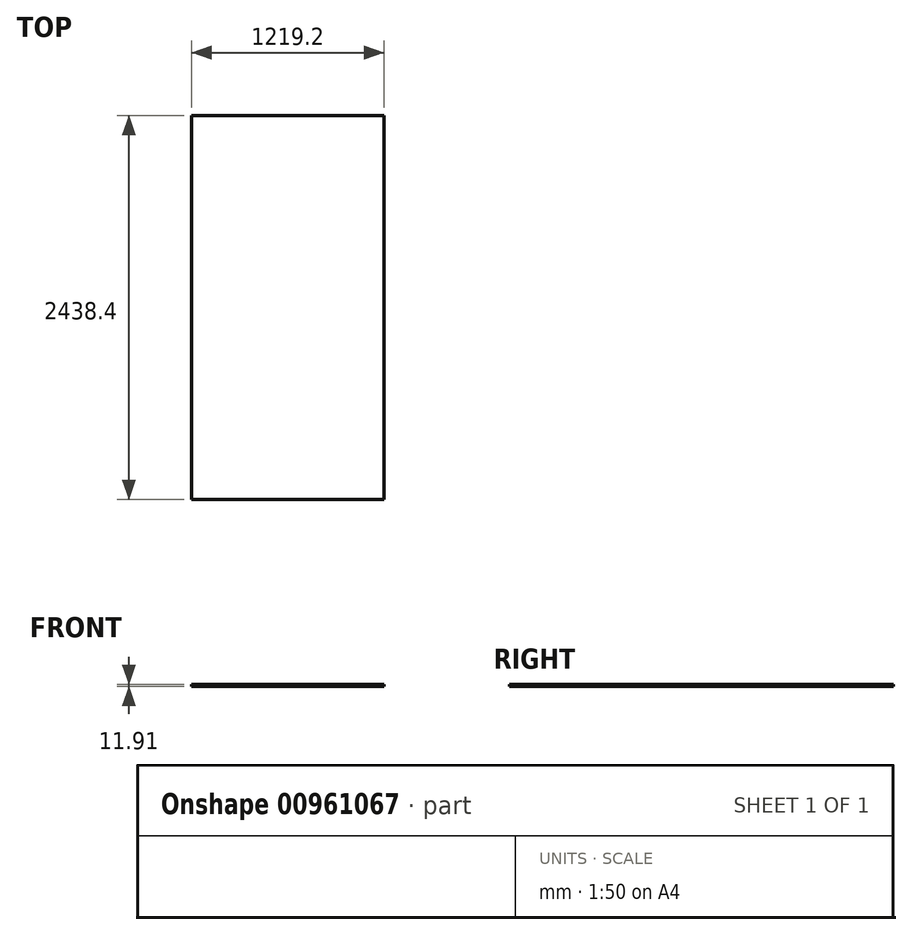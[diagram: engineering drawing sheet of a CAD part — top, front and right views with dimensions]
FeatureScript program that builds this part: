
annotation { "Feature Type Name" : "Feature", "Feature Type Description" : "" }
export const myFeature = defineFeature(function(context is Context, id is Id, definition is map)
    precondition{}
    {
        {
            var Q0;
            Q0=qCreatedBy(makeId("Front.planeOp"),FACE);
            var sketch = newSketch(context, id + "F0", { "sketchPlane" : qUnion([Q0])});
            skLineSegment(sketch, "E0.bottom", {"start": v(-366.63, 36.44) * mm, "end": v(852.57, 36.44) * mm});
            skLineSegment(sketch, "E0.top", {"start": v(-366.63, 48.35) * mm, "end": v(852.57, 48.35) * mm});
            skLineSegment(sketch, "E0.left", {"start": v(-366.63, 36.44) * mm, "end": v(-366.63, 48.35) * mm});
            skLineSegment(sketch, "E0.right", {"start": v(852.57, 36.44) * mm, "end": v(852.57, 48.35) * mm});
            skLineSegment(sketch, "E1.bottom", {"start": v(-1762, 47.6) * mm, "end": v(-542.8, 47.6) * mm});
            skLineSegment(sketch, "E1.top", {"start": v(-1762, 59.5) * mm, "end": v(-542.8, 59.5) * mm});
            skLineSegment(sketch, "E1.left", {"start": v(-1762, 47.6) * mm, "end": v(-1762, 59.5) * mm});
            skLineSegment(sketch, "E1.right", {"start": v(-542.8, 47.6) * mm, "end": v(-542.8, 59.5) * mm});
            skSolve(sketch);
        }
        {
            var Q0;
            Q0=makeQuery(id+"F0.imprint","IMPRINT",FACE,{"disambiguationData":[TD([[makeQuery(id+"F0.imprint","IMPRINT",EDGE,{"derivedFrom":sQuery(id+"F0.wireOp",EDGE,"E0.bottom")}),1.0]])]});
            extrude(context, id + "F1", {"entities" : qUnion([Q0]), "depth" : 2438.4 * mm, "offsetDistance" : 25.4 * mm});
        }
    });
